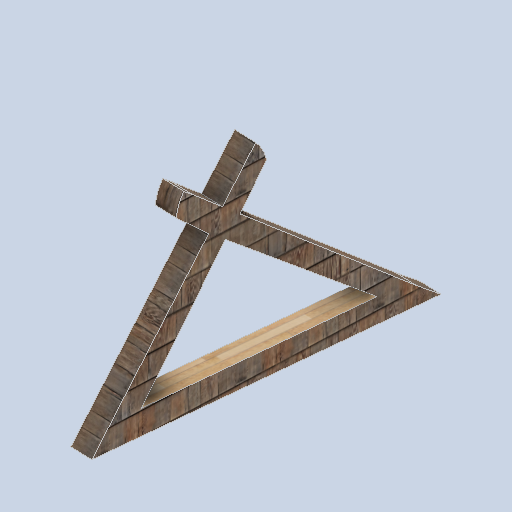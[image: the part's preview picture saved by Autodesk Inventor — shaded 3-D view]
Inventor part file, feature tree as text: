
AUTODESK INVENTOR PART (.ipt)
format: ipt  version: 2024.2 (Build 282272000, 272)  size: 220,160 bytes
history: native  units: in
note: dims shown in document units (in); Inventor stores cm internally (conversion verified against a paired STEP export)
features: sketch x9, plane x6, other x3
ambient origin geometry x8: Origin, YZ Plane, XZ Plane, XY Plane, X Axis, Y Axis, Z Axis, Center Point
bodies: Solid1 (feature_tree)
feature tree (18):
  other  "pad_outframe_03.ipt"
  other  "Solid1::pad_outframe_03.ipt"
  other  "TaggingFeature1"
  sketch  "Sketch1"  dims[d0=0.3937in]
  sketch  "Sketch2"
  sketch  "Sketch3"
  sketch  "Sketch6"
  sketch  "Sketch7"
  sketch  "Sketch8"
  sketch  "Sketch9"
  sketch  "Sketch10"
  sketch  "Sketch11"
  plane  "Work Plane1"
  plane  "Work Plane2"
  plane  "Work Plane3"
  plane  "Work Plane4"
  plane  "Work Plane5"
  plane  "Work Plane6"
